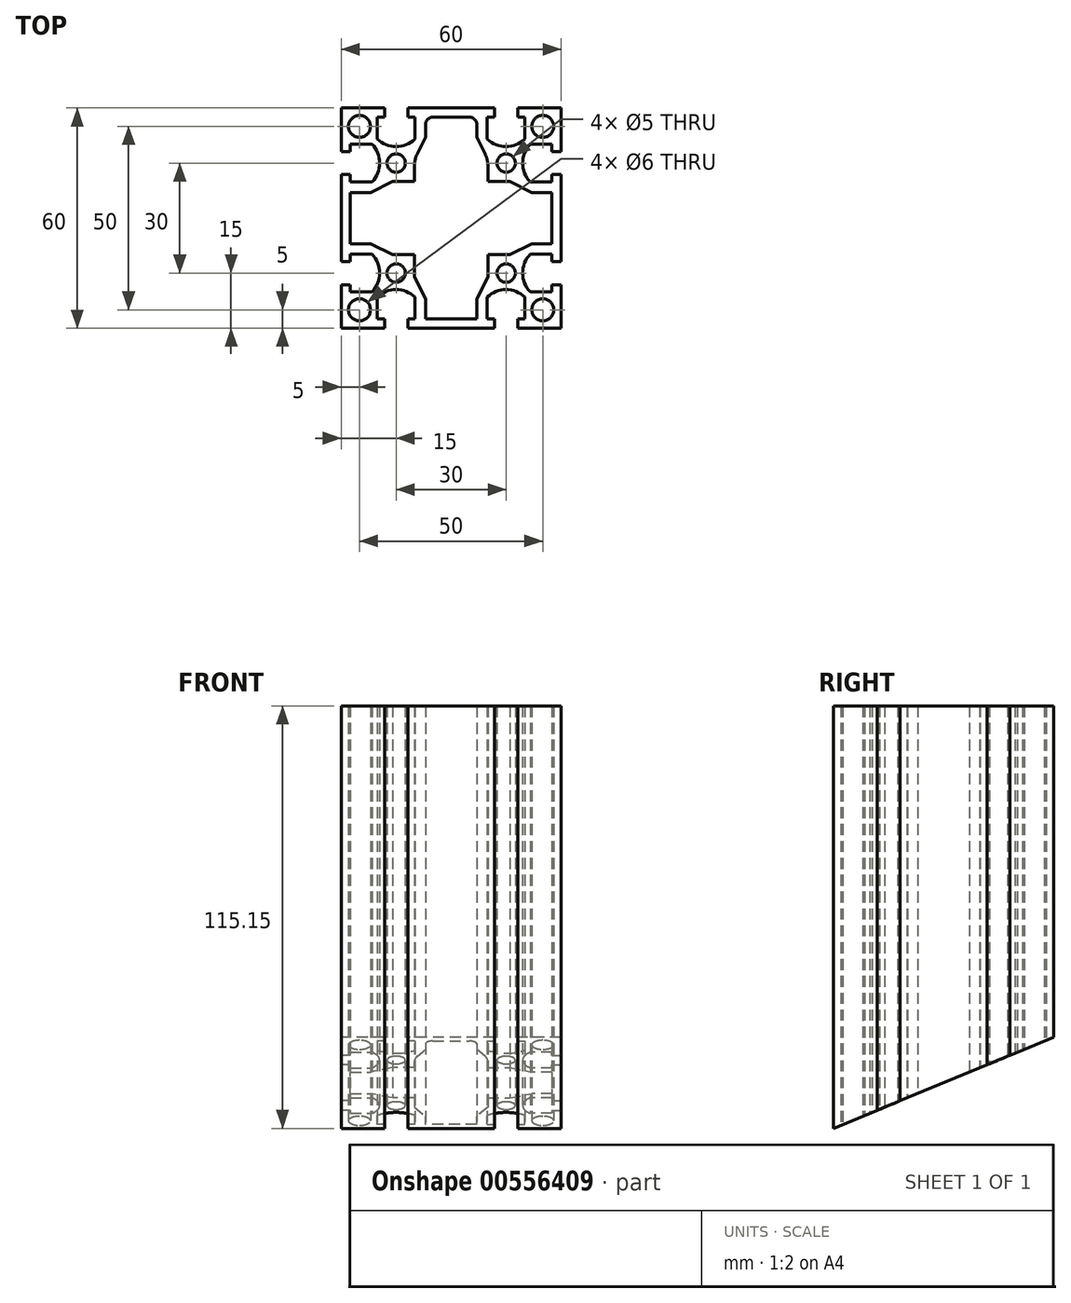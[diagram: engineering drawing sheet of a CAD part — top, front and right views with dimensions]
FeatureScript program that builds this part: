
annotation { "Feature Type Name" : "Feature", "Feature Type Description" : "" }
export const myFeature = defineFeature(function(context is Context, id is Id, definition is map)
    precondition{}
    {
        {
            var Q0;
            Q0=qCreatedBy(makeId("Top.planeOp"),FACE);
            var sketch = newSketch(context, id + "F0", { "sketchPlane" : qUnion([Q0])});
            skLineSegment(sketch, "E0.bottom", {"start": v(30, -30) * mm, "end": v(-30, -30) * mm});
            skLineSegment(sketch, "E0.top", {"start": v(30, 30) * mm, "end": v(-30, 30) * mm});
            skLineSegment(sketch, "E0.left", {"start": v(30, -30) * mm, "end": v(30, 30) * mm});
            skLineSegment(sketch, "E0.right", {"start": v(-30, -30) * mm, "end": v(-30, 30) * mm});
            skPoint(sketch, "E0.middle", {"position": v(0, 0) * mm});
            skLineSegment(sketch, "E1.top", {"start": v(-11.85, 30) * mm, "end": v(-18.15, 30) * mm});
            skLineSegment(sketch, "E1.left", {"start": v(-11.85, 27.5) * mm, "end": v(-11.85, 30) * mm});
            skLineSegment(sketch, "E1.right", {"start": v(-18.15, 27.5) * mm, "end": v(-18.15, 30) * mm});
            skPoint(sketch, "E1.middle", {"position": v(-15, 28.75) * mm});
            skLineSegment(sketch, "E2.bottom", {"start": v(-9.85, 27.5) * mm, "end": v(-11.85, 27.5) * mm});
            skLineSegment(sketch, "E2.left", {"start": v(-9.85, 27.5) * mm, "end": v(-9.85, 21.55) * mm});
            skLineSegment(sketch, "E2.right", {"start": v(-20.15, 27.5) * mm, "end": v(-20.15, 21.55) * mm});
            skPoint(sketch, "E2.middle", {"position": v(-15, 24.52) * mm});
            skArc(sketch, "E3", {"start": v(-20.15, 21.55) * mm, "mid": v(-15, 19.5) * mm, "end": v(-9.85, 21.55) * mm});
            skPoint(sketch, "E4.MirrorP", {"position": v(15, 24.52) * mm});
            skPoint(sketch, "E5.MirrorP", {"position": v(15, 28.75) * mm});
            skLineSegment(sketch, "E6.MirrorCS", {"start": v(11.85, 27.5) * mm, "end": v(11.85, 30) * mm});
            skLineSegment(sketch, "E7.MirrorCS", {"start": v(18.15, 27.5) * mm, "end": v(18.15, 30) * mm});
            skLineSegment(sketch, "E8.MirrorCS", {"start": v(9.85, 27.5) * mm, "end": v(11.85, 27.5) * mm});
            skLineSegment(sketch, "E9.MirrorCS", {"start": v(9.85, 27.5) * mm, "end": v(9.85, 21.55) * mm});
            skArc(sketch, "E10.MirrorCS", {"start": v(20.15, 21.55) * mm, "mid": v(15, 19.5) * mm, "end": v(9.85, 21.55) * mm});
            skLineSegment(sketch, "E11.MirrorCS", {"start": v(20.15, 27.5) * mm, "end": v(20.15, 21.55) * mm});
            skLineSegment(sketch, "E12.MirrorCS", {"start": v(11.85, 30) * mm, "end": v(18.15, 30) * mm});
            skLineSegment(sketch, "E13.1.0", {"start": v(27.5, 20.15) * mm, "end": v(21.55, 20.15) * mm});
            skLineSegment(sketch, "E13.1.1", {"start": v(27.5, 9.85) * mm, "end": v(21.55, 9.85) * mm});
            skArc(sketch, "E13.1.2", {"start": v(21.55, 20.15) * mm, "mid": v(19.5, 15) * mm, "end": v(21.55, 9.85) * mm});
            skLineSegment(sketch, "E13.1.3", {"start": v(27.5, -9.85) * mm, "end": v(21.55, -9.85) * mm});
            skLineSegment(sketch, "E13.1.4", {"start": v(27.5, -20.15) * mm, "end": v(21.55, -20.15) * mm});
            skPoint(sketch, "E13.1.5", {"position": v(28.75, 15) * mm});
            skPoint(sketch, "E13.1.6", {"position": v(28.75, -15) * mm});
            skArc(sketch, "E13.1.7", {"start": v(21.55, -20.15) * mm, "mid": v(19.5, -15) * mm, "end": v(21.55, -9.85) * mm});
            skPoint(sketch, "E13.1.8", {"position": v(24.52, -15) * mm});
            skPoint(sketch, "E13.1.9", {"position": v(24.52, 15) * mm});
            skLineSegment(sketch, "E13.1.10", {"start": v(27.5, 9.85) * mm, "end": v(27.5, 20.15) * mm});
            skLineSegment(sketch, "E13.1.11", {"start": v(27.5, -11.85) * mm, "end": v(27.5, -18.15) * mm});
            skLineSegment(sketch, "E13.1.12", {"start": v(30, 11.85) * mm, "end": v(30, 18.15) * mm});
            skLineSegment(sketch, "E13.1.13", {"start": v(30, -11.85) * mm, "end": v(30, -18.15) * mm});
            skLineSegment(sketch, "E13.1.14", {"start": v(27.5, 18.15) * mm, "end": v(30, 18.15) * mm});
            skLineSegment(sketch, "E13.1.15", {"start": v(27.5, 11.85) * mm, "end": v(30, 11.85) * mm});
            skLineSegment(sketch, "E13.1.16", {"start": v(27.5, 11.85) * mm, "end": v(27.5, 18.15) * mm});
            skLineSegment(sketch, "E13.1.17", {"start": v(27.5, -9.85) * mm, "end": v(27.5, -20.15) * mm});
            skLineSegment(sketch, "E13.1.18", {"start": v(27.5, -18.15) * mm, "end": v(30, -18.15) * mm});
            skLineSegment(sketch, "E13.1.19", {"start": v(27.5, -11.85) * mm, "end": v(30, -11.85) * mm});
            skLineSegment(sketch, "E13.2.0", {"start": v(20.15, -27.5) * mm, "end": v(20.15, -21.55) * mm});
            skLineSegment(sketch, "E13.2.1", {"start": v(9.85, -27.5) * mm, "end": v(9.85, -21.55) * mm});
            skArc(sketch, "E13.2.2", {"start": v(20.15, -21.55) * mm, "mid": v(15, -19.5) * mm, "end": v(9.85, -21.55) * mm});
            skLineSegment(sketch, "E13.2.3", {"start": v(-9.85, -27.5) * mm, "end": v(-9.85, -21.55) * mm});
            skLineSegment(sketch, "E13.2.4", {"start": v(-20.15, -27.5) * mm, "end": v(-20.15, -21.55) * mm});
            skPoint(sketch, "E13.2.5", {"position": v(15, -28.75) * mm});
            skPoint(sketch, "E13.2.6", {"position": v(-15, -28.75) * mm});
            skArc(sketch, "E13.2.7", {"start": v(-20.15, -21.55) * mm, "mid": v(-15, -19.5) * mm, "end": v(-9.85, -21.55) * mm});
            skPoint(sketch, "E13.2.8", {"position": v(-15, -24.52) * mm});
            skPoint(sketch, "E13.2.9", {"position": v(15, -24.52) * mm});
            skLineSegment(sketch, "E13.2.10", {"start": v(9.85, -27.5) * mm, "end": v(20.15, -27.5) * mm});
            skLineSegment(sketch, "E13.2.11", {"start": v(-11.85, -27.5) * mm, "end": v(-18.15, -27.5) * mm});
            skLineSegment(sketch, "E13.2.12", {"start": v(11.85, -30) * mm, "end": v(18.15, -30) * mm});
            skLineSegment(sketch, "E13.2.13", {"start": v(-11.85, -30) * mm, "end": v(-18.15, -30) * mm});
            skLineSegment(sketch, "E13.2.14", {"start": v(18.15, -27.5) * mm, "end": v(18.15, -30) * mm});
            skLineSegment(sketch, "E13.2.15", {"start": v(11.85, -27.5) * mm, "end": v(11.85, -30) * mm});
            skLineSegment(sketch, "E13.2.16", {"start": v(11.85, -27.5) * mm, "end": v(18.15, -27.5) * mm});
            skLineSegment(sketch, "E13.2.17", {"start": v(-9.85, -27.5) * mm, "end": v(-20.15, -27.5) * mm});
            skLineSegment(sketch, "E13.2.18", {"start": v(-18.15, -27.5) * mm, "end": v(-18.15, -30) * mm});
            skLineSegment(sketch, "E13.2.19", {"start": v(-11.85, -27.5) * mm, "end": v(-11.85, -30) * mm});
            skLineSegment(sketch, "E13.3.0", {"start": v(-27.5, -20.15) * mm, "end": v(-21.55, -20.15) * mm});
            skLineSegment(sketch, "E13.3.1", {"start": v(-27.5, -9.85) * mm, "end": v(-21.55, -9.85) * mm});
            skArc(sketch, "E13.3.2", {"start": v(-21.55, -20.15) * mm, "mid": v(-19.5, -15) * mm, "end": v(-21.55, -9.85) * mm});
            skLineSegment(sketch, "E13.3.3", {"start": v(-27.5, 9.85) * mm, "end": v(-21.55, 9.85) * mm});
            skLineSegment(sketch, "E13.3.4", {"start": v(-27.5, 20.15) * mm, "end": v(-21.55, 20.15) * mm});
            skPoint(sketch, "E13.3.5", {"position": v(-28.75, -15) * mm});
            skPoint(sketch, "E13.3.6", {"position": v(-28.75, 15) * mm});
            skArc(sketch, "E13.3.7", {"start": v(-21.55, 20.15) * mm, "mid": v(-19.5, 15) * mm, "end": v(-21.55, 9.85) * mm});
            skPoint(sketch, "E13.3.8", {"position": v(-24.52, 15) * mm});
            skPoint(sketch, "E13.3.9", {"position": v(-24.52, -15) * mm});
            skLineSegment(sketch, "E13.3.10", {"start": v(-27.5, -9.85) * mm, "end": v(-27.5, -20.15) * mm});
            skLineSegment(sketch, "E13.3.11", {"start": v(-27.5, 11.85) * mm, "end": v(-27.5, 18.15) * mm});
            skLineSegment(sketch, "E13.3.12", {"start": v(-30, -11.85) * mm, "end": v(-30, -18.15) * mm});
            skLineSegment(sketch, "E13.3.13", {"start": v(-30, 11.85) * mm, "end": v(-30, 18.15) * mm});
            skLineSegment(sketch, "E13.3.14", {"start": v(-27.5, -18.15) * mm, "end": v(-30, -18.15) * mm});
            skLineSegment(sketch, "E13.3.15", {"start": v(-27.5, -11.85) * mm, "end": v(-30, -11.85) * mm});
            skLineSegment(sketch, "E13.3.16", {"start": v(-27.5, -11.85) * mm, "end": v(-27.5, -18.15) * mm});
            skLineSegment(sketch, "E13.3.17", {"start": v(-27.5, 9.85) * mm, "end": v(-27.5, 20.15) * mm});
            skLineSegment(sketch, "E13.3.18", {"start": v(-27.5, 18.15) * mm, "end": v(-30, 18.15) * mm});
            skLineSegment(sketch, "E13.3.19", {"start": v(-27.5, 11.85) * mm, "end": v(-30, 11.85) * mm});
            skLineSegment(sketch, "E13.anchor1", {"start": v(0, 0) * mm, "end": v(-20.15, 21.55) * mm, "construction": true});
            skLineSegment(sketch, "E13.anchor2", {"start": v(0, 0) * mm, "end": v(-21.55, -20.15) * mm, "construction": true});
            skLineSegment(sketch, "E14.trimOffspring", {"start": v(-18.15, 27.5) * mm, "end": v(-20.15, 27.5) * mm});
            skLineSegment(sketch, "E15.trimOffspring", {"start": v(18.15, 27.5) * mm, "end": v(20.15, 27.5) * mm});
            skCircle(sketch, "E16", {"center": v(-15, 15) * mm, "radius": 2.5 * mm});
            skCircle(sketch, "E17", {"center": v(-25, 25) * mm, "radius": 3 * mm});
            skCircle(sketch, "E18.MirrorC", {"center": v(25, 25) * mm, "radius": 3 * mm});
            skCircle(sketch, "E19.MirrorC", {"center": v(25, -25) * mm, "radius": 3 * mm});
            skCircle(sketch, "E20.MirrorC", {"center": v(-25, -25) * mm, "radius": 3 * mm});
            skCircle(sketch, "E21.MirrorC", {"center": v(15, 15) * mm, "radius": 2.5 * mm});
            skCircle(sketch, "E22.MirrorC", {"center": v(15, -15) * mm, "radius": 2.5 * mm});
            skCircle(sketch, "E23.MirrorC", {"center": v(-15, -15) * mm, "radius": 2.5 * mm});
            skLineSegment(sketch, "E24", {"start": v(-7, 27.5) * mm, "end": v(0, 27.5) * mm});
            skLineSegment(sketch, "E25", {"start": v(-7, 27.5) * mm, "end": v(-7, 22) * mm});
            skLineSegment(sketch, "E26", {"start": v(-10, 10) * mm, "end": v(-10, 16) * mm});
            skLineSegment(sketch, "E27", {"start": v(-10, 16) * mm, "end": v(-7, 22) * mm});
            skLineSegment(sketch, "E28.MirrorCS", {"start": v(10, 10) * mm, "end": v(10, 16) * mm});
            skLineSegment(sketch, "E29.MirrorCS", {"start": v(10, 16) * mm, "end": v(7, 22) * mm});
            skLineSegment(sketch, "E30.MirrorCS", {"start": v(7, 27.5) * mm, "end": v(0, 27.5) * mm});
            skLineSegment(sketch, "E31.MirrorCS", {"start": v(7, 27.5) * mm, "end": v(7, 22) * mm});
            skLineSegment(sketch, "E32.1.0", {"start": v(-10, -10) * mm, "end": v(-16, -10) * mm});
            skLineSegment(sketch, "E32.1.1", {"start": v(-16, -10) * mm, "end": v(-22, -7) * mm});
            skLineSegment(sketch, "E32.1.2", {"start": v(-27.5, -7) * mm, "end": v(-22, -7) * mm});
            skLineSegment(sketch, "E32.1.3", {"start": v(-27.5, -7) * mm, "end": v(-27.5, 0) * mm});
            skLineSegment(sketch, "E32.1.4", {"start": v(-27.5, 7) * mm, "end": v(-27.5, 0) * mm});
            skLineSegment(sketch, "E32.1.5", {"start": v(-27.5, 7) * mm, "end": v(-22, 7) * mm});
            skLineSegment(sketch, "E32.1.6", {"start": v(-16, 10) * mm, "end": v(-22, 7) * mm});
            skLineSegment(sketch, "E32.1.7", {"start": v(-10, 10) * mm, "end": v(-16, 10) * mm});
            skLineSegment(sketch, "E32.2.0", {"start": v(10, -10) * mm, "end": v(10, -16) * mm});
            skLineSegment(sketch, "E32.2.1", {"start": v(10, -16) * mm, "end": v(7, -22) * mm});
            skLineSegment(sketch, "E32.2.2", {"start": v(7, -27.5) * mm, "end": v(7, -22) * mm});
            skLineSegment(sketch, "E32.2.3", {"start": v(7, -27.5) * mm, "end": v(0, -27.5) * mm});
            skLineSegment(sketch, "E32.2.4", {"start": v(-7, -27.5) * mm, "end": v(0, -27.5) * mm});
            skLineSegment(sketch, "E32.2.5", {"start": v(-7, -27.5) * mm, "end": v(-7, -22) * mm});
            skLineSegment(sketch, "E32.2.6", {"start": v(-10, -16) * mm, "end": v(-7, -22) * mm});
            skLineSegment(sketch, "E32.2.7", {"start": v(-10, -10) * mm, "end": v(-10, -16) * mm});
            skLineSegment(sketch, "E32.3.0", {"start": v(10, 10) * mm, "end": v(16, 10) * mm});
            skLineSegment(sketch, "E32.3.1", {"start": v(16, 10) * mm, "end": v(22, 7) * mm});
            skLineSegment(sketch, "E32.3.2", {"start": v(27.5, 7) * mm, "end": v(22, 7) * mm});
            skLineSegment(sketch, "E32.3.3", {"start": v(27.5, 7) * mm, "end": v(27.5, 0) * mm});
            skLineSegment(sketch, "E32.3.4", {"start": v(27.5, -7) * mm, "end": v(27.5, 0) * mm});
            skLineSegment(sketch, "E32.3.5", {"start": v(27.5, -7) * mm, "end": v(22, -7) * mm});
            skLineSegment(sketch, "E32.3.6", {"start": v(16, -10) * mm, "end": v(22, -7) * mm});
            skLineSegment(sketch, "E32.3.7", {"start": v(10, -10) * mm, "end": v(16, -10) * mm});
            skSolve(sketch);
        }
        {
            var Q0;
            {var subQ30=sQuery(id+"F0.wireOp",EDGE,"E1.left");Q0=makeQuery(id+"F0.imprint","IMPRINT",FACE,{"disambiguationData":[TD([[makeQuery(id+"F0.imprint","IMPRINT",EDGE,{"derivedFrom":subQ30}),-1.0]])]});}
            extrude(context, id + "F1", {"entities" : qUnion([Q0]), "depth" : 140 * mm, "offsetDistance" : 25 * mm});
        }
        {
            var Q0;
            Q0=makeQuery(id+"F1.opExtrude","SWEPT_EDGE",EDGE,{"disambiguationData":[OSD([sQuery(id+"F0.wireOp",EDGE,"E24"),sQuery(id+"F0.wireOp",EDGE,"E25")])]});
            var Q1;
            Q1=makeQuery(id+"F1.opExtrude","SWEPT_EDGE",EDGE,{"disambiguationData":[OSD([sQuery(id+"F0.wireOp",EDGE,"E30.MirrorCS"),sQuery(id+"F0.wireOp",EDGE,"E31.MirrorCS")])]});
            var Q2;
            Q2=makeQuery(id+"F1.opExtrude","SWEPT_EDGE",EDGE,{"disambiguationData":[OSD([sQuery(id+"F0.wireOp",EDGE,"840db5bc-c403-45cd-90c7-254e62d9e8c5.3.2"),sQuery(id+"F0.wireOp",EDGE,"840db5bc-c403-45cd-90c7-254e62d9e8c5.3.3")])]});
            var Q3;
            Q3=makeQuery(id+"F1.opExtrude","SWEPT_EDGE",EDGE,{"disambiguationData":[OSD([sQuery(id+"F0.wireOp",EDGE,"840db5bc-c403-45cd-90c7-254e62d9e8c5.3.4"),sQuery(id+"F0.wireOp",EDGE,"840db5bc-c403-45cd-90c7-254e62d9e8c5.3.5")])]});
            var Q4;
            Q4=makeQuery(id+"F1.opExtrude","SWEPT_EDGE",EDGE,{"disambiguationData":[OSD([sQuery(id+"F0.wireOp",EDGE,"840db5bc-c403-45cd-90c7-254e62d9e8c5.1.4"),sQuery(id+"F0.wireOp",EDGE,"840db5bc-c403-45cd-90c7-254e62d9e8c5.1.5")])]});
            var Q5;
            Q5=makeQuery(id+"F1.opExtrude","SWEPT_EDGE",EDGE,{"disambiguationData":[OSD([sQuery(id+"F0.wireOp",EDGE,"840db5bc-c403-45cd-90c7-254e62d9e8c5.1.2"),sQuery(id+"F0.wireOp",EDGE,"840db5bc-c403-45cd-90c7-254e62d9e8c5.1.3")])]});
            var Q6;
            Q6=makeQuery(id+"F1.opExtrude","SWEPT_EDGE",EDGE,{"disambiguationData":[OSD([sQuery(id+"F0.wireOp",EDGE,"840db5bc-c403-45cd-90c7-254e62d9e8c5.2.2"),sQuery(id+"F0.wireOp",EDGE,"840db5bc-c403-45cd-90c7-254e62d9e8c5.2.3")])]});
            var Q7;
            Q7=makeQuery(id+"F1.opExtrude","SWEPT_EDGE",EDGE,{"disambiguationData":[OSD([sQuery(id+"F0.wireOp",EDGE,"840db5bc-c403-45cd-90c7-254e62d9e8c5.2.4"),sQuery(id+"F0.wireOp",EDGE,"840db5bc-c403-45cd-90c7-254e62d9e8c5.2.5")])]});
            fillet(context, id + "F2", {"entities" : qUnion([Q0, Q1, Q2, Q3, Q4, Q5, Q6, Q7]), "radius" : 2 * mm, "tangentPropagation" : true, "allowEdgeOverflow" : false});
        }
        {
            var Q0;
            Q0=makeQuery(id+"F1.opExtrude","SWEPT_EDGE",EDGE,{"disambiguationData":[OSD([sQuery(id+"F0.wireOp",EDGE,"E26"),sQuery(id+"F0.wireOp",EDGE,"E27")])]});
            var Q1;
            Q1=makeQuery(id+"F1.opExtrude","SWEPT_EDGE",EDGE,{"disambiguationData":[OSD([sQuery(id+"F0.wireOp",EDGE,"E28.MirrorCS"),sQuery(id+"F0.wireOp",EDGE,"E29.MirrorCS")])]});
            var Q2;
            Q2=makeQuery(id+"F1.opExtrude","SWEPT_EDGE",EDGE,{"disambiguationData":[OSD([sQuery(id+"F0.wireOp",EDGE,"840db5bc-c403-45cd-90c7-254e62d9e8c5.3.0"),sQuery(id+"F0.wireOp",EDGE,"840db5bc-c403-45cd-90c7-254e62d9e8c5.3.1")])]});
            var Q3;
            Q3=makeQuery(id+"F1.opExtrude","SWEPT_EDGE",EDGE,{"disambiguationData":[OSD([sQuery(id+"F0.wireOp",EDGE,"840db5bc-c403-45cd-90c7-254e62d9e8c5.1.6"),sQuery(id+"F0.wireOp",EDGE,"840db5bc-c403-45cd-90c7-254e62d9e8c5.1.7")])]});
            var Q4;
            Q4=makeQuery(id+"F1.opExtrude","SWEPT_EDGE",EDGE,{"disambiguationData":[OSD([sQuery(id+"F0.wireOp",EDGE,"840db5bc-c403-45cd-90c7-254e62d9e8c5.1.0"),sQuery(id+"F0.wireOp",EDGE,"840db5bc-c403-45cd-90c7-254e62d9e8c5.1.1")])]});
            var Q5;
            Q5=makeQuery(id+"F1.opExtrude","SWEPT_EDGE",EDGE,{"disambiguationData":[OSD([sQuery(id+"F0.wireOp",EDGE,"840db5bc-c403-45cd-90c7-254e62d9e8c5.3.6"),sQuery(id+"F0.wireOp",EDGE,"840db5bc-c403-45cd-90c7-254e62d9e8c5.3.7")])]});
            var Q6;
            Q6=makeQuery(id+"F1.opExtrude","SWEPT_EDGE",EDGE,{"disambiguationData":[OSD([sQuery(id+"F0.wireOp",EDGE,"840db5bc-c403-45cd-90c7-254e62d9e8c5.2.0"),sQuery(id+"F0.wireOp",EDGE,"840db5bc-c403-45cd-90c7-254e62d9e8c5.2.1")])]});
            var Q7;
            Q7=makeQuery(id+"F1.opExtrude","SWEPT_EDGE",EDGE,{"disambiguationData":[OSD([sQuery(id+"F0.wireOp",EDGE,"840db5bc-c403-45cd-90c7-254e62d9e8c5.2.6"),sQuery(id+"F0.wireOp",EDGE,"840db5bc-c403-45cd-90c7-254e62d9e8c5.2.7")])]});
            fillet(context, id + "F3", {"entities" : qUnion([Q0, Q1, Q2, Q3, Q4, Q5, Q6, Q7]), "radius" : 7 * mm, "tangentPropagation" : true, "allowEdgeOverflow" : false});
        }
        {
            var Q0;
            {var subQ0=sQuery(id+"F0.wireOp",EDGE,"E0.bottom");Q0=makeQuery(id+"F1.opExtrude","SWEPT_FACE",FACE,{"disambiguationData":[OSD([subQ0]),TDD([makeQuery(id+"F0.imprint","IMPRINT",EDGE,{"disambiguationData":[TD([[makeQuery(id+"F0.imprint","INTERSECT",VERTEX,{"derivedFrom":[subQ0,sQuery(id+"F0.wireOp",EDGE,"E13.2.12"),sQuery(id+"F0.wireOp",EDGE,"E13.2.15")]}),-1.0]])],"derivedFrom":subQ0})])]});}
            var sketch = newSketch(context, id + "F4", { "sketchPlane" : qUnion([Q0])});
            skLineSegment(sketch, "E33.0", {"start": v(-18.15, 140) * mm, "end": v(-30, 140) * mm});
            skLineSegment(sketch, "E33.1", {"start": v(30, 140) * mm, "end": v(30, 0) * mm});
            skLineSegment(sketch, "E34", {"start": v(-30, 140) * mm, "end": v(30, 140) * mm});
            skLineSegment(sketch, "E35", {"start": v(30, 80) * mm, "end": v(-30, 140) * mm});
            skLineSegment(sketch, "E36.0", {"start": v(-18.15, 0) * mm, "end": v(-30, 0) * mm});
            skLineSegment(sketch, "E37", {"start": v(-30, 0) * mm, "end": v(30, 0) * mm});
            skLineSegment(sketch, "E38", {"start": v(30, 60) * mm, "end": v(-30, 0) * mm});
            skSolve(sketch);
        }
        {
            var Q0;
            Q0=qCreatedBy(makeId("Right.planeOp"),FACE);
            var sketch = newSketch(context, id + "F5", { "sketchPlane" : qUnion([Q0])});
            skLineSegment(sketch, "E39.bottom", {"start": v(130.97, 66.67) * mm, "end": v(-30, 0) * mm});
            skLineSegment(sketch, "E39.top", {"start": v(214.6, -135.23) * mm, "end": v(53.63, -201.9) * mm});
            skLineSegment(sketch, "E39.left", {"start": v(130.97, 66.67) * mm, "end": v(214.6, -135.23) * mm});
            skLineSegment(sketch, "E39.right", {"start": v(-30, 0) * mm, "end": v(53.63, -201.9) * mm});
            skLineSegment(sketch, "E40.bottom", {"start": v(-2, 217.27) * mm, "end": v(-162.34, 150.86) * mm});
            skLineSegment(sketch, "E40.top", {"start": v(30, 140) * mm, "end": v(-130.33, 73.59) * mm});
            skLineSegment(sketch, "E40.left", {"start": v(-2, 217.27) * mm, "end": v(30, 140) * mm});
            skLineSegment(sketch, "E40.right", {"start": v(-162.34, 150.86) * mm, "end": v(-130.33, 73.59) * mm});
            skSolve(sketch);
        }
        {
            var Q0;
            Q0=makeQuery(id+"F5.imprint","IMPRINT",FACE,{"disambiguationData":[TD([[makeQuery(id+"F5.imprint","IMPRINT",EDGE,{"derivedFrom":sQuery(id+"F5.wireOp",EDGE,"E39.bottom")}),1.0]])]});
            var Q1;
            Q1=makeQuery(id+"F5.imprint","IMPRINT",FACE,{"disambiguationData":[TD([[makeQuery(id+"F5.imprint","IMPRINT",EDGE,{"derivedFrom":sQuery(id+"F5.wireOp",EDGE,"E40.bottom")}),1.0]])]});
            extrude(context, id + "F6", {"entities" : qUnion([Q0, Q1]), "operationType" : NewBodyOperationType.REMOVE, "oppositeDirection" : true, "depth" : 30 * mm, "offsetDistance" : 25 * mm, "hasSecondDirection" : true, "secondDirectionOppositeDirection" : false, "secondDirectionDepth" : 30 * mm});
        }
        {
            var Q0;
            Q0=qCreatedBy(makeId("Right.planeOp"),FACE);
            var sketch = newSketch(context, id + "F7", { "sketchPlane" : qUnion([Q0])});
            skLineSegment(sketch, "E41.bottom", {"start": v(101.16, 165.85) * mm, "end": v(-30, 165.85) * mm});
            skLineSegment(sketch, "E41.top", {"start": v(101.16, 115.15) * mm, "end": v(-30, 115.15) * mm});
            skLineSegment(sketch, "E41.left", {"start": v(101.16, 165.85) * mm, "end": v(101.16, 115.15) * mm});
            skLineSegment(sketch, "E41.right", {"start": v(-30, 165.85) * mm, "end": v(-30, 115.15) * mm});
            skSolve(sketch);
        }
        {
            var Q0;
            Q0=qSketchRegion(id+"F7",true);
            extrude(context, id + "F8", {"entities" : qUnion([Q0]), "operationType" : NewBodyOperationType.REMOVE, "depth" : 30 * mm, "offsetDistance" : 25 * mm, "hasSecondDirection" : true, "secondDirectionOppositeDirection" : true, "secondDirectionDepth" : 30 * mm});
        }
    });
